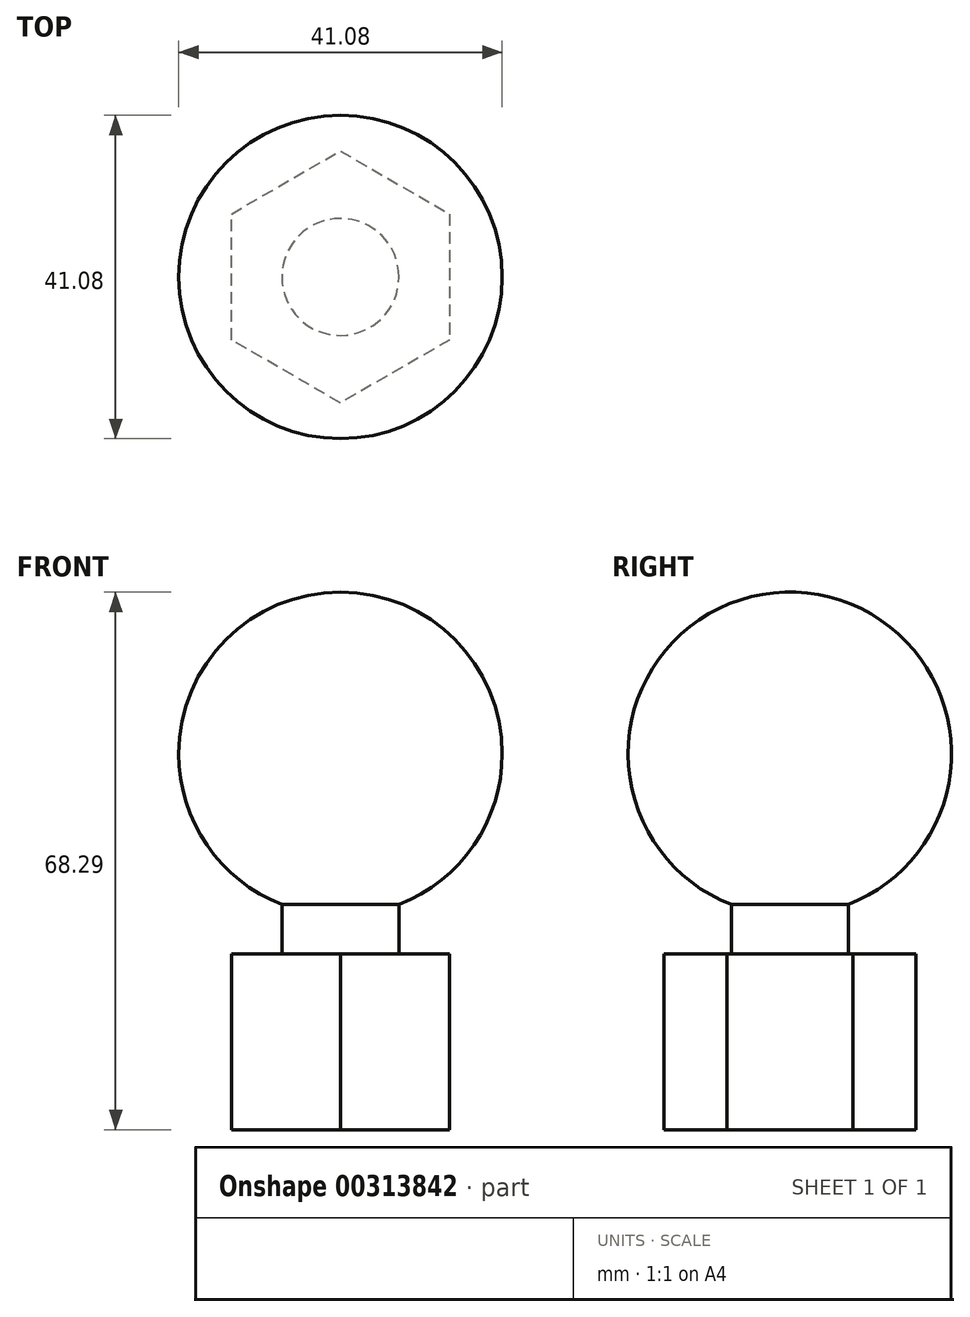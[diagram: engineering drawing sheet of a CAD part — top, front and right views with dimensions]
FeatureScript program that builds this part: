
annotation { "Feature Type Name" : "Feature", "Feature Type Description" : "" }
export const myFeature = defineFeature(function(context is Context, id is Id, definition is map)
    precondition{}
    {
        {
            var Q0;
            Q0=qCreatedBy(makeId("Top.planeOp"),FACE);
            var sketch = newSketch(context, id + "F0", { "sketchPlane" : qUnion([Q0])});
            skCircle(sketch, "E0.cCircle", {"center": v(0, 0) * mm, "radius": 13.86 * mm, "construction": true});
            skLineSegment(sketch, "E0.0", {"start": v(13.86, 8) * mm, "end": v(13.86, -8) * mm});
            skLineSegment(sketch, "E0.1", {"start": v(13.86, -8) * mm, "end": v(0, -16) * mm});
            skLineSegment(sketch, "E0.2", {"start": v(0, -16) * mm, "end": v(-13.86, -8) * mm});
            skLineSegment(sketch, "E0.3", {"start": v(-13.86, -8) * mm, "end": v(-13.86, 8) * mm});
            skLineSegment(sketch, "E0.4", {"start": v(-13.86, 8) * mm, "end": v(0, 16) * mm});
            skLineSegment(sketch, "E0.5", {"start": v(0, 16) * mm, "end": v(13.86, 8) * mm});
            skPoint(sketch, "E0.0.midPoint", {"position": v(13.86, 0) * mm});
            skSolve(sketch);
        }
        {
            var Q0;
            Q0 = qSketchRegion(id + "F0", true);
            extrude(context, id + "F1", {"entities" : qUnion([Q0]), "depth" : 22.35 * mm});
        }
        {
            var Q0;
            Q0=makeQuery(id+"F1.opExtrude","CAP_FACE",FACE,{"disambiguationData":[OSD([sQuery(id+"F0.wireOp",EDGE,"E0.0"),sQuery(id+"F0.wireOp",EDGE,"E0.1"),sQuery(id+"F0.wireOp",EDGE,"E0.2"),sQuery(id+"F0.wireOp",EDGE,"E0.3"),sQuery(id+"F0.wireOp",EDGE,"E0.4"),sQuery(id+"F0.wireOp",EDGE,"E0.5")])],"isStart":false});
            var sketch = newSketch(context, id + "F2", { "sketchPlane" : qUnion([Q0])});
            skCircle(sketch, "E1", {"center": v(0, 0) * mm, "radius": 7.43 * mm});
            skSolve(sketch);
        }
        {
            var Q0;
            Q0 = qSketchRegion(id + "F2", true);
            extrude(context, id + "F3", {"entities" : qUnion([Q0]), "operationType" : NewBodyOperationType.ADD, "depth" : 25.4 * mm});
        }
        {
            var Q0;
            Q0=makeQuery(id+"F3.opExtrude","CAP_FACE",FACE,{"disambiguationData":[OSD([sQuery(id+"F2.wireOp",EDGE,"E1")])],"isStart":false});
            var sketch = newSketch(context, id + "F4", { "sketchPlane" : qUnion([Q0])});
            skArc(sketch, "E2", {"start": v(20.54, 0) * mm, "mid": v(0, 20.54) * mm, "end": v(-20.54, 0) * mm});
            skLineSegment(sketch, "E3", {"start": v(20.54, 0) * mm, "end": v(-20.54, 0) * mm});
            skPoint(sketch, "E4.orphan", {"position": v(24.3, 0) * mm});
            skSolve(sketch);
        }
        {
            var Q0;
            {var subQ0=sQuery(id+"F4.wireOp",EDGE,"E2");Q0=makeQuery(id+"F4.imprint","IMPRINT",FACE,{"disambiguationData":[TD([[makeQuery(id+"F4.imprint","IMPRINT",EDGE,{"derivedFrom":subQ0}),1.0]])]});}
            var Q1;
            {var subQ0=sQuery(id+"F4.wireOp",EDGE,"E3");var subQ1=makeQuery(id+"F3.opExtrude","CAP_EDGE",EDGE,{"disambiguationData":[OSD([sQuery(id+"F2.wireOp",EDGE,"E1")])],"isStart":false});var subQ2=makeQuery(id+"F4.imprint","INTERSECT",VERTEX,{"disambiguationData":[OD(0.0)],"derivedFrom":[subQ1,subQ0]});Q1=makeQuery(id+"F4.imprint","IMPRINT",FACE,{"disambiguationData":[TD([[makeQuery(id+"F4.imprint","IMPRINT",EDGE,{"disambiguationData":[TD([[subQ2,-1.0]])],"derivedFrom":subQ0}),-1.0]])]});}
            var Q2;
            Q2=sQuery(id+"F4.wireOp",EDGE,"E3");
            revolve(context, id + "F5", {"operationType" : NewBodyOperationType.ADD, "entities" : qUnion([Q0, Q1]), "axis" : qUnion([Q2]), "revolveType" : RevolveType.FULL});
        }
    });
